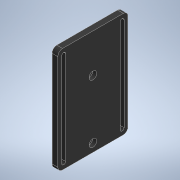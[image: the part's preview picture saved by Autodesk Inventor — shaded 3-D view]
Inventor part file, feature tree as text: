
AUTODESK INVENTOR PART (.ipt)
format: ipt  version: 2022.2 (Build 262287010, 287A)  size: 135,168 bytes
history: native  units: mm
features: sketch x3, extrude x2, hole x1, mirror x1, fillet x1
ambient origin geometry x8: Origin, YZ Plane, XZ Plane, XY Plane, X Axis, Y Axis, Z Axis, Center Point
bodies: Volumenkörper1 (feature_tree)
feature tree (8):
  extrude  "Extrusion1"  Depth=3.3mm
  hole  "Bohrung1"  [1 undecoded]
  extrude  "Extrusion2"  Depth=5.0mm TaperAngle=0.0deg
  mirror  "Spiegeln1"
  fillet  "Rundung1"  Radius=90.0mm
  sketch  "Skizze1"  dims[d4=5.0mm d5=0.0mm]
  sketch  "Skizze2"  dims[d7=3.4mm d8=6.0mm d9=6.5mm d10=3.4mm d11=90.0deg d12=8.0mm d13=20.594885mm d14=3.3mm]
  sketch  "Skizze3"  dims[d15=80.0mm d16=25.0mm d17=5.0mm d18=0.0mm d21=90.0mm d22=60.0mm d23=50.0mm d24=7.0mm d25=4.0mm]
note: 1 required parameter value undecoded (feature->parameter linkage not recoverable at this tier; creation-order binding heuristic only, values carry confidence <= 0.55)
